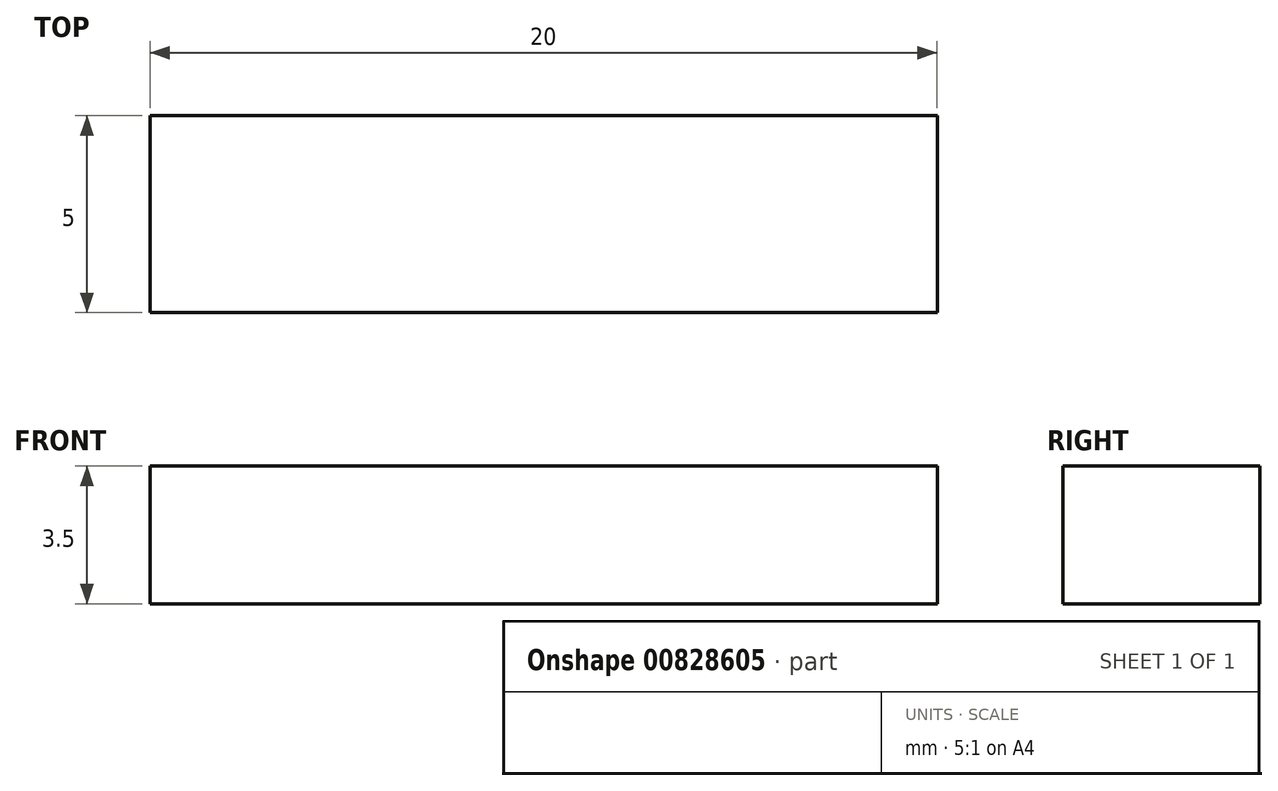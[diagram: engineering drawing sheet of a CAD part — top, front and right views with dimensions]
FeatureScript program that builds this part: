
annotation { "Feature Type Name" : "Feature", "Feature Type Description" : "" }
export const myFeature = defineFeature(function(context is Context, id is Id, definition is map)
    precondition{}
    {
        {
            var Q0;
            Q0=qCreatedBy(makeId("Top.planeOp"),FACE);
            var sketch = newSketch(context, id + "F0", { "sketchPlane" : qUnion([Q0])});
            skLineSegment(sketch, "E0.bottom", {"start": v(-46.47, 12.56) * mm, "end": v(-26.47, 12.56) * mm});
            skLineSegment(sketch, "E0.top", {"start": v(-46.47, 7.56) * mm, "end": v(-26.47, 7.56) * mm});
            skLineSegment(sketch, "E0.left", {"start": v(-46.47, 12.56) * mm, "end": v(-46.47, 7.56) * mm});
            skLineSegment(sketch, "E0.right", {"start": v(-26.47, 12.56) * mm, "end": v(-26.47, 7.56) * mm});
            skSolve(sketch);
        }
        {
            var Q0;
            Q0 = qSketchRegion(id + "F0", true);
            extrude(context, id + "F1", {"entities" : qUnion([Q0]), "depth" : 3.5 * mm, "offsetDistance" : 25 * mm});
        }
    });
